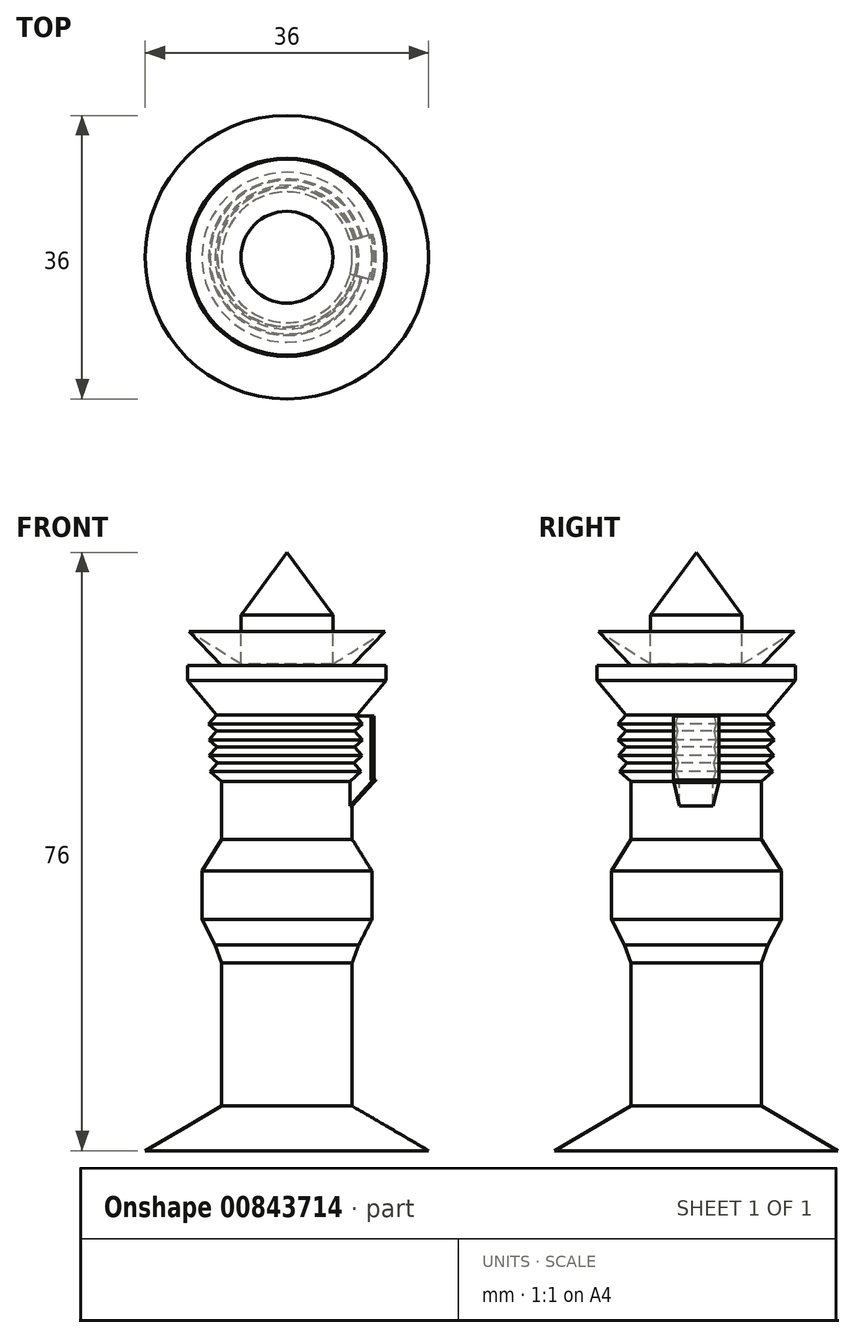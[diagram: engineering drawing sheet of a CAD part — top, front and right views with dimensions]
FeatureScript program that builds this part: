
annotation { "Feature Type Name" : "Feature", "Feature Type Description" : "" }
export const myFeature = defineFeature(function(context is Context, id is Id, definition is map)
    precondition{}
    {
        {
            var Q0;
            Q0=qCreatedBy(makeId("Front.planeOp"),FACE);
            var sketch = newSketch(context, id + "F0", { "sketchPlane" : qUnion([Q0])});
            skLineSegment(sketch, "E0", {"start": v(0, -18.72) * mm, "end": v(18, -18.72) * mm});
            skPoint(sketch, "E1.start.orphan", {"position": v(19.65, -8.94) * mm});
            skPoint(sketch, "E2.start.orphan", {"position": v(15.62, 5.16) * mm});
            skPoint(sketch, "E3.start.orphan", {"position": v(15.62, 29.32) * mm});
            skPoint(sketch, "E4.start.orphan", {"position": v(15.62, 37.23) * mm});
            skPoint(sketch, "E5.start.orphan", {"position": v(15.62, 33.34) * mm});
            skPoint(sketch, "E6.start.orphan", {"position": v(19.65, 44.62) * mm});
            skPoint(sketch, "E7.start.orphan", {"position": v(9.4, 37.23) * mm});
            skLineSegment(sketch, "E8", {"start": v(18, -18.72) * mm, "end": v(12.58, -15.55) * mm});
            skLineSegment(sketch, "E9", {"start": v(12.58, -15.55) * mm, "end": v(8.3, -13.06) * mm});
            skLineSegment(sketch, "E10", {"start": v(8.3, -13.06) * mm, "end": v(8.3, -4.8) * mm});
            skLineSegment(sketch, "E11", {"start": v(8.3, -4.8) * mm, "end": v(8.3, 1.68) * mm});
            skLineSegment(sketch, "E12", {"start": v(8.3, 1.68) * mm, "end": v(8.3, 5.16) * mm});
            skLineSegment(sketch, "E13", {"start": v(8.3, 5.16) * mm, "end": v(9.13, 7.45) * mm});
            skLineSegment(sketch, "E14", {"start": v(9.13, 7.45) * mm, "end": v(10.8, 10.65) * mm});
            skLineSegment(sketch, "E15", {"start": v(10.8, 10.65) * mm, "end": v(10.8, 16.8) * mm});
            skLineSegment(sketch, "E16", {"start": v(10.8, 16.8) * mm, "end": v(8.3, 20.83) * mm});
            skLineSegment(sketch, "E17", {"start": v(8.3, 20.83) * mm, "end": v(8.3, 28.17) * mm});
            skLineSegment(sketch, "E18", {"start": v(8.3, 28.17) * mm, "end": v(9.74, 29.45) * mm});
            skLineSegment(sketch, "E19", {"start": v(9.74, 29.45) * mm, "end": v(8.8, 30.51) * mm});
            skLineSegment(sketch, "E20", {"start": v(8.8, 30.51) * mm, "end": v(9.87, 31.47) * mm});
            skLineSegment(sketch, "E21", {"start": v(9.87, 31.47) * mm, "end": v(8.9, 32.56) * mm});
            skLineSegment(sketch, "E22", {"start": v(8.9, 32.56) * mm, "end": v(9.91, 33.46) * mm});
            skLineSegment(sketch, "E23", {"start": v(9.91, 33.46) * mm, "end": v(8.9, 34.6) * mm});
            skLineSegment(sketch, "E24", {"start": v(8.9, 34.6) * mm, "end": v(9.93, 35.5) * mm});
            skLineSegment(sketch, "E25", {"start": v(9.93, 35.5) * mm, "end": v(8.9, 36.65) * mm});
            skLineSegment(sketch, "E26", {"start": v(8.9, 36.65) * mm, "end": v(12.61, 41.01) * mm});
            skLineSegment(sketch, "E27", {"start": v(12.61, 41.01) * mm, "end": v(12.61, 42.94) * mm});
            skLineSegment(sketch, "E28", {"start": v(12.61, 42.94) * mm, "end": v(8.3, 42.94) * mm});
            skLineSegment(sketch, "E29", {"start": v(8.3, 42.94) * mm, "end": v(12.44, 47.2) * mm});
            skLineSegment(sketch, "E30", {"start": v(12.44, 47.2) * mm, "end": v(5.83, 43.1) * mm});
            skLineSegment(sketch, "E31", {"start": v(5.83, 43.1) * mm, "end": v(5.83, 49.3) * mm});
            skLineSegment(sketch, "E32", {"start": v(5.83, 49.3) * mm, "end": v(0, 57.28) * mm});
            skLineSegment(sketch, "E33", {"start": v(0, 57.28) * mm, "end": v(0, -18.72) * mm});
            skSolve(sketch);
        }
        {
            var Q0;
            Q0=qCreatedBy(makeId("Front.planeOp"),FACE);
            var sketch = newSketch(context, id + "F1", { "sketchPlane" : qUnion([Q0])});
            skLineSegment(sketch, "E34.bottom", {"start": v(7.1, 36.52) * mm, "end": v(11.1, 36.52) * mm});
            skLineSegment(sketch, "E34.top", {"start": v(7.1, 28.06) * mm, "end": v(11.1, 28.06) * mm});
            skLineSegment(sketch, "E34.left", {"start": v(7.1, 36.52) * mm, "end": v(7.1, 28.06) * mm});
            skLineSegment(sketch, "E34.right", {"start": v(11.1, 36.52) * mm, "end": v(11.1, 28.06) * mm});
            skLineSegment(sketch, "E35", {"start": v(0, 36.76) * mm, "end": v(0, 24.94) * mm});
            skSolve(sketch);
        }
        {
            var Q0;
            Q0 = qSketchRegion(id + "F0", true);
            var Q1;
            Q1=sQuery(id+"F0.wireOp",EDGE,"E33");
            revolve(context, id + "F2", {"surfaceOperationType" : NewSurfaceOperationType.NEW, "entities" : qUnion([Q0]), "axis" : qUnion([Q1]), "revolveType" : RevolveType.FULL});
        }
        {
            var Q0;
            Q0=makeQuery(id+"F1.imprint","IMPRINT",FACE,{"disambiguationData":[TD([[makeQuery(id+"F1.imprint","IMPRINT",EDGE,{"derivedFrom":sQuery(id+"F1.wireOp",EDGE,"E34.bottom")}),-1.0]])]});
            var Q1;
            Q1=sQuery(id+"F1.wireOp",EDGE,"E35");
            revolve(context, id + "F3", {"operationType" : NewBodyOperationType.ADD, "surfaceOperationType" : NewSurfaceOperationType.NEW, "entities" : qUnion([Q0]), "axis" : qUnion([Q1]), "revolveType" : RevolveType.SYMMETRIC, "angle" : 30 * degree});
        }
        {
            var Q0;
            Q0=qCreatedBy(makeId("Front.planeOp"),FACE);
            var sketch = newSketch(context, id + "F4", { "sketchPlane" : qUnion([Q0])});
            skLineSegment(sketch, "E36", {"start": v(11.33, 28.38) * mm, "end": v(8.2, 24.95) * mm});
            skLineSegment(sketch, "E37", {"start": v(8.2, 24.95) * mm, "end": v(8.2, 28.5) * mm});
            skLineSegment(sketch, "E38", {"start": v(8.2, 28.5) * mm, "end": v(11.33, 28.38) * mm});
            skSolve(sketch);
        }
        {
            var Q0;
            Q0 = qSketchRegion(id + "F4", true);
            var Q1;
            Q1=sQuery(id+"F1.wireOp",EDGE,"E35");
            revolve(context, id + "F5", {"operationType" : NewBodyOperationType.ADD, "surfaceOperationType" : NewSurfaceOperationType.NEW, "entities" : qUnion([Q0]), "axis" : qUnion([Q1]), "revolveType" : RevolveType.SYMMETRIC, "angle" : 30 * degree});
        }
    });
